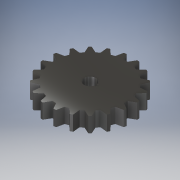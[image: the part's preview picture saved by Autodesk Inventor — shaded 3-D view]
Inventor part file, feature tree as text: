
AUTODESK INVENTOR PART (.ipt)
format: ipt  version: 2019 (Build 230136000, 136)  size: 206,848 bytes
history: native  units: mm
features: extrude x3, sketch x2, plane x1, pattern_circular x1
ambient origin geometry x8: Origin, YZ Plane, XZ Plane, XY Plane, X Axis, Y Axis, Z Axis, Center Point
bodies: Solid1 (feature_tree)
feature tree (7):
  sketch  "Sketch1"  dims[d1=150.0mm d5=30.0deg]
  plane  "Work Plane1"
  extrude  "Extrusion4"  TaperAngle=30.0deg  [1 undecoded]
  extrude  "Extrusion5"  Depth=1250.0mm TaperAngle=0.0deg
  pattern_circular  "Circular Pattern2"  Count=125  [1 undecoded]
  extrude  "Extrusion7"  Depth=1250.0mm TaperAngle=360.0deg
  sketch  "Sketch3"  dims[d20=150.0mm d24=1250.0mm d25=0.0mm d26=1250.0mm d27=0.0mm d28=200.0mm d29=360.0deg d37=1250.0mm d38=0.0mm]
note: 2 required parameter values undecoded (feature->parameter linkage not recoverable at this tier; creation-order binding heuristic only, values carry confidence <= 0.55)
